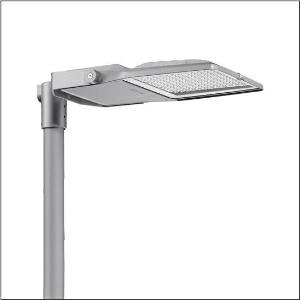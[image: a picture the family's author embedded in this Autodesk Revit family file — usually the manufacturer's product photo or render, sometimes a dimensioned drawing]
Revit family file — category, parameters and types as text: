
# Revit family: floodlight_fl_21_iq_midi___pl64_5xa7782e4e3a_6d1b
name_source: partatom
category: Lighting Fixtures
units: mm (PartAtom-declared; Revit-internal decimal feet)

## family parameters
Cut with Voids When Loaded = No
Host = Face
Light Source = No
Part Type = Normal
Room Calculation Point = No
Round Connector Dimension = Use Diameter
Shared = No

## types (1)
- --- (1 x LED, 27050 lm, 208.1 W, 4000K)
    Apparent Load = 208 VA
    CIE Flux Codes = 28 80 98 100 100
    Color Rendering = 70
    Color Temperature = 4000K
    Default Elevation = 1800 mm
    Description = Floodlight FL 21 iQ midi, floodlight, primary light control with lens, of PMMA, primary optical cover: protective disc, of toughened safety glass, transparent, light distribution: PL64, light emission: direct distribution, installation type: surface-mounted, lamps: LED, High Power LED, rated values: 27.050lm | 208,1W | 130lm/W (begin service life); end service life: 27.050lm | 227,1W; at 50% lumin. flux: 13.525lm | 90,3W | 149,8lm/W, colour temperature: 4000K, colour rendering: CRI > 70, light colour: 740, light setting 1 begin service life: 100% | 27.050lm | 208,1W | 130lm/W | 4.000K, light setting 1 end service life: 227,1W, further light settings possible, control: optimised constant luminous flux control (CLO 2.0), Desk-Remote (wireless, voltage-free reading and setting of iQ features in the workshop via application-optimized NFC function/RFID function), Smart-Wire, Night-Set, Temp-Guard, Auto-Match, Street-Remote, pre-setting: linear dimming characteristic, with terminal, 6-pole, mains connection: 220..240V, AC, 50/60Hz, luminaire housing, of diecast aluminium, powder-coated, SITECO metallic grey (DB 702S), corrosivity category C5 mid according to DIN EN ISO 12944suitable for swimming poolschlorine-resistant, sealing non-destructively replaceable, please order mast flange separately, mast bracket, of steel, galvanised, powder-coated, SITECO metallic grey (DB 702S), protection rating (complete): IP66, insulation class (complete): insulation class II (safety insulation), certification: CE, ENEC, VDE, protection symbol: D, impact resistance: IK08, permissible operating ambient temperature: -40..+40°C, permissible operating ambient temperature for outdoor applications: -40..+50°C, standard: DIN EN 12944, LABS conformity tested according to VDMA 24364:2018-05, packaging unit: 1 piece

Light Distribution: PL64
    Height = 76 mm
    Lamp = 1 x LED
    Lamp Light Flux = 27050 lm
    Lamp Power = 208.1 W
    Lamp count = 1
    Length = 657 mm
    Luminous efficacy = 130 lm/W
    Manufacturer = Siteco
    ModVariant = No
    Model = 5XA7782E4E3A
    Mounting Place = Pole
    Mounting Type = Pole annexe
    Number of Poles = 1
    OnlyDefault = Yes
    Power Factor = 1
    Product Name = Floodlight FL 21 iQ midi | PL64
    Product group = floodlight | pylon annexe
    ProductGroupID = 6201
    Protection Class = Protection class II
    Protection Degree = IP 66
    RLX_Detail_Level = 1
    RLX_Emergency_Light_Flux = 0 lm
    RLX_Emergency_Type = 0
    RLX_Emergency_Type_DB = No
    RlxData = <blob elided: 153845 chars, md5=1709a777>
    Socket = socket
    Standby Power = 0 W
    System Light Flux = 27050 lm
    System Power = 208 W
    Type Comments = factory setting: luminous flux: 100 % | dim-lin: 254 | 710 mA
    Type Image = l_1007123.jpg
    URL = http://relux.com
    VarID = @adj_108483
    Voltage = 0 V
    Weight = 0.00 kg
    Width = 442 mm

## geometry (parser evidence)
native form markers: Blend x4, Sweep x11
no freeform markers — native parametric forms only
